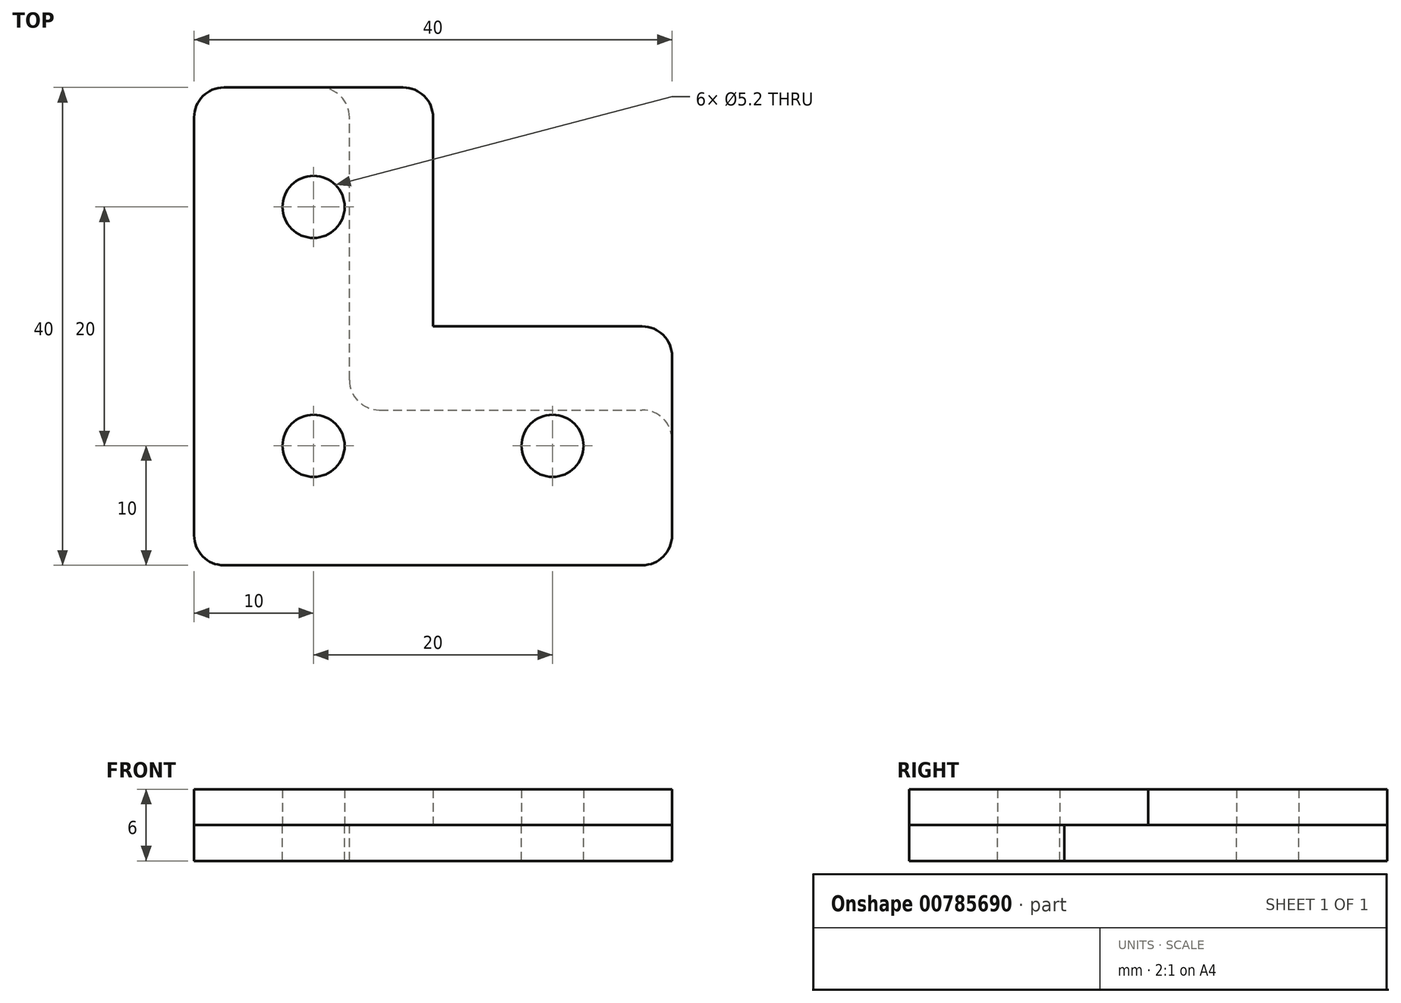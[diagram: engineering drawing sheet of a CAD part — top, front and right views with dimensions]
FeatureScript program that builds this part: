
annotation { "Feature Type Name" : "Feature", "Feature Type Description" : "" }
export const myFeature = defineFeature(function(context is Context, id is Id, definition is map)
    precondition{}
    {
        {
            var Q0;
            Q0=qCreatedBy(makeId("Top.planeOp"),FACE);
            var sketch = newSketch(context, id + "F0", { "sketchPlane" : qUnion([Q0])});
            skLineSegment(sketch, "E0.bottom", {"start": v(17.5, -20) * mm, "end": v(-17.5, -20) * mm});
            skLineSegment(sketch, "E0.top", {"start": v(-2.5, 20) * mm, "end": v(-17.5, 20) * mm});
            skLineSegment(sketch, "E0.left", {"start": v(20, -17.5) * mm, "end": v(20, -2.5) * mm});
            skLineSegment(sketch, "E0.right", {"start": v(-20, -17.5) * mm, "end": v(-20, 17.5) * mm});
            skPoint(sketch, "E0.middle", {"position": v(0, 0) * mm});
            skLineSegment(sketch, "E1.top", {"start": v(0, 0) * mm, "end": v(17.5, 0) * mm});
            skLineSegment(sketch, "E1.left", {"start": v(0, 17.5) * mm, "end": v(0, 0) * mm});
            skPoint(sketch, "E2.orphan", {"position": v(20, 20) * mm});
            skPoint(sketch, "E3.visualSharp", {"position": v(-20, 20) * mm});
            skArc(sketch, "E3.filletArc", {"start": v(-17.5, 20) * mm, "mid": v(-19.27, 19.27) * mm, "end": v(-20, 17.5) * mm});
            skPoint(sketch, "E4.visualSharp", {"position": v(-20, -20) * mm});
            skArc(sketch, "E4.filletArc", {"start": v(-20, -17.5) * mm, "mid": v(-19.27, -19.27) * mm, "end": v(-17.5, -20) * mm});
            skPoint(sketch, "E5.visualSharp", {"position": v(20, -20) * mm});
            skArc(sketch, "E5.filletArc", {"start": v(17.5, -20) * mm, "mid": v(19.27, -19.27) * mm, "end": v(20, -17.5) * mm});
            skPoint(sketch, "E6.visualSharp", {"position": v(20, 0) * mm});
            skArc(sketch, "E6.filletArc", {"start": v(20, -2.5) * mm, "mid": v(19.27, -0.73) * mm, "end": v(17.5, 0) * mm});
            skPoint(sketch, "E7.visualSharp", {"position": v(0, 20) * mm});
            skArc(sketch, "E7.filletArc", {"start": v(0, 17.5) * mm, "mid": v(-0.73, 19.27) * mm, "end": v(-2.5, 20) * mm});
            skLineSegment(sketch, "E8", {"start": v(-10, 20) * mm, "end": v(-10, -20) * mm, "construction": true});
            skLineSegment(sketch, "E9", {"start": v(20, -10) * mm, "end": v(-20, -10) * mm, "construction": true});
            skCircle(sketch, "E10", {"center": v(-10, -10) * mm, "radius": 2.6 * mm});
            skCircle(sketch, "E11", {"center": v(-10, 10) * mm, "radius": 2.6 * mm});
            skCircle(sketch, "E12", {"center": v(10, -10) * mm, "radius": 2.6 * mm});
            skSolve(sketch);
        }
        {
            var Q0;
            Q0=makeQuery(id+"F0.imprint","IMPRINT",FACE,{"disambiguationData":[TD([[makeQuery(id+"F0.imprint","IMPRINT",EDGE,{"derivedFrom":sQuery(id+"F0.wireOp",EDGE,"E0.bottom")}),-1.0]])]});
            extrude(context, id + "F1", {"entities" : qUnion([Q0]), "depth" : 3 * mm, "offsetDistance" : 25 * mm});
        }
        {
            var Q0;
            Q0=makeQuery(id+"F1.opExtrude","CAP_FACE",FACE,{"disambiguationData":[OSD([sQuery(id+"F0.wireOp",EDGE,"E0.bottom"),sQuery(id+"F0.wireOp",EDGE,"E0.top"),sQuery(id+"F0.wireOp",EDGE,"E0.left"),sQuery(id+"F0.wireOp",EDGE,"E0.right"),sQuery(id+"F0.wireOp",EDGE,"E1.top"),sQuery(id+"F0.wireOp",EDGE,"E1.left"),sQuery(id+"F0.wireOp",EDGE,"E3.filletArc"),sQuery(id+"F0.wireOp",EDGE,"E4.filletArc"),sQuery(id+"F0.wireOp",EDGE,"E5.filletArc"),sQuery(id+"F0.wireOp",EDGE,"E6.filletArc"),sQuery(id+"F0.wireOp",EDGE,"E7.filletArc"),sQuery(id+"F0.wireOp",EDGE,"E10"),sQuery(id+"F0.wireOp",EDGE,"E11"),sQuery(id+"F0.wireOp",EDGE,"E12")])],"isStart":true});
            var sketch = newSketch(context, id + "F2", { "sketchPlane" : qUnion([Q0])});
            skLineSegment(sketch, "E13.bottom", {"start": v(-4.5, 7) * mm, "end": v(17.5, 7) * mm});
            skLineSegment(sketch, "E13.left", {"start": v(-7, 4.5) * mm, "end": v(-7, -17.5) * mm});
            skPoint(sketch, "E14.visualSharp", {"position": v(-7, 7) * mm});
            skArc(sketch, "E14.filletArc", {"start": v(-4.5, 7) * mm, "mid": v(-6.27, 6.27) * mm, "end": v(-7, 4.5) * mm});
            skLineSegment(sketch, "E15.0", {"start": v(17.5, 20) * mm, "end": v(-17.5, 20) * mm});
            skArc(sketch, "E16.0", {"start": v(-20, 17.5) * mm, "mid": v(-19.27, 19.27) * mm, "end": v(-17.5, 20) * mm});
            skLineSegment(sketch, "E17.0", {"start": v(-20, 17.5) * mm, "end": v(-20, -17.5) * mm});
            skArc(sketch, "E18.0", {"start": v(-17.5, -20) * mm, "mid": v(-19.27, -19.27) * mm, "end": v(-20, -17.5) * mm});
            skLineSegment(sketch, "E19.0", {"start": v(-9.5, -20) * mm, "end": v(-17.5, -20) * mm});
            skArc(sketch, "E20.0", {"start": v(17.5, 20) * mm, "mid": v(19.27, 19.27) * mm, "end": v(20, 17.5) * mm});
            skLineSegment(sketch, "E21.0", {"start": v(20, 17.5) * mm, "end": v(20, 9.5) * mm});
            skPoint(sketch, "E22.orphan", {"position": v(20, 2.5) * mm});
            skPoint(sketch, "E23.orphan", {"position": v(-2.5, -20) * mm});
            skPoint(sketch, "E24.visualSharp", {"position": v(-7, -20) * mm});
            skArc(sketch, "E24.filletArc", {"start": v(-9.5, -20) * mm, "mid": v(-7.73, -19.27) * mm, "end": v(-7, -17.5) * mm});
            skPoint(sketch, "E25.visualSharp", {"position": v(20, 7) * mm});
            skArc(sketch, "E25.filletArc", {"start": v(17.5, 7) * mm, "mid": v(19.27, 7.73) * mm, "end": v(20, 9.5) * mm});
            skCircle(sketch, "E26", {"center": v(-10, 10) * mm, "radius": 2.6 * mm});
            skCircle(sketch, "E27", {"center": v(10, 10) * mm, "radius": 2.6 * mm});
            skCircle(sketch, "E28", {"center": v(-10, -10) * mm, "radius": 2.6 * mm});
            skSolve(sketch);
        }
        {
            var Q0;
            Q0=makeQuery(id+"F2.imprint","IMPRINT",FACE,{"disambiguationData":[TD([[makeQuery(id+"F2.imprint","IMPRINT",EDGE,{"derivedFrom":sQuery(id+"F2.wireOp",EDGE,"E13.bottom")}),1.0]])]});
            extrude(context, id + "F3", {"entities" : qUnion([Q0]), "depth" : 3 * mm, "offsetDistance" : 25 * mm});
        }
    });
